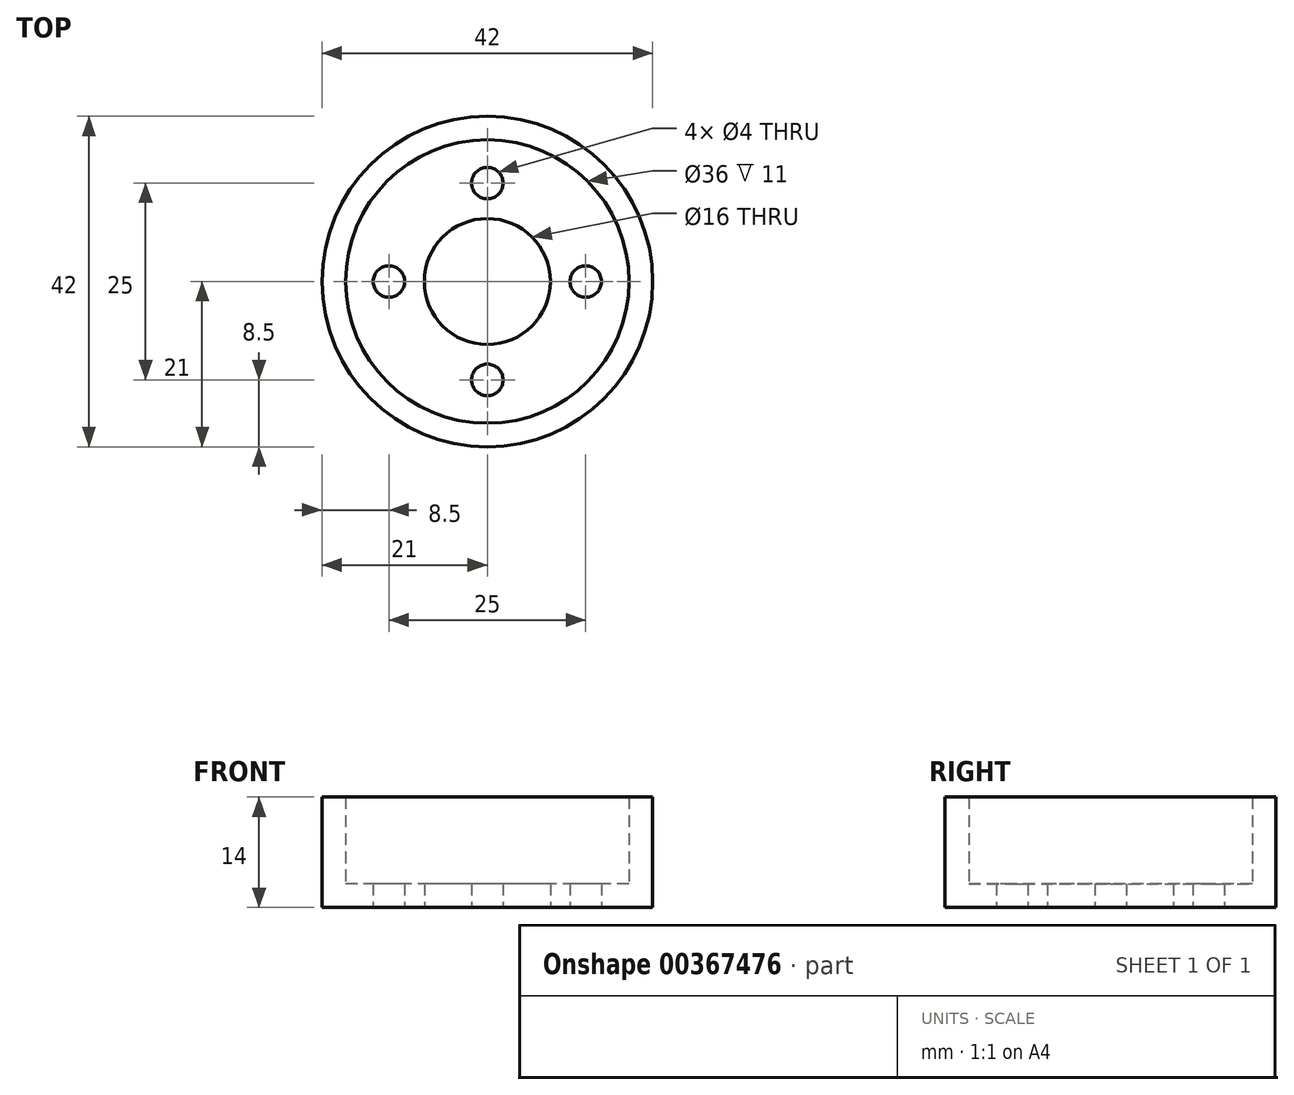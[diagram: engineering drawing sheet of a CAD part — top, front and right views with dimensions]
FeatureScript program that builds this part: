
annotation { "Feature Type Name" : "Feature", "Feature Type Description" : "" }
export const myFeature = defineFeature(function(context is Context, id is Id, definition is map)
    precondition{}
    {
        {
            var Q0;
            Q0=qCreatedBy(makeId("Top.planeOp"),FACE);
            var sketch = newSketch(context, id + "F0", { "sketchPlane" : qUnion([Q0])});
            skLineSegment(sketch, "E0", {"start": v(0, 0) * mm, "end": v(12.5, 0) * mm});
            skCircle(sketch, "E1", {"center": v(12.5, 0) * mm, "radius": 2 * mm});
            skLineSegment(sketch, "E2", {"start": v(0, 0) * mm, "end": v(0, -12.5) * mm});
            skCircle(sketch, "E3", {"center": v(0, -12.5) * mm, "radius": 2 * mm});
            skLineSegment(sketch, "E4", {"start": v(0, 0) * mm, "end": v(0, 12.5) * mm});
            skCircle(sketch, "E5", {"center": v(0, 12.5) * mm, "radius": 2 * mm});
            skLineSegment(sketch, "E6", {"start": v(0, 0) * mm, "end": v(-12.5, 0) * mm});
            skCircle(sketch, "E7", {"center": v(-12.5, 0) * mm, "radius": 2 * mm});
            skSolve(sketch);
        }
        {
            var Q0;
            Q0=qCreatedBy(makeId("Top.planeOp"),FACE);
            var sketch = newSketch(context, id + "F1", { "sketchPlane" : qUnion([Q0])});
            skCircle(sketch, "E8", {"center": v(0, 0) * mm, "radius": 8 * mm});
            skSolve(sketch);
        }
        {
            var Q0;
            Q0=qCreatedBy(makeId("Top.planeOp"),FACE);
            var sketch = newSketch(context, id + "F2", { "sketchPlane" : qUnion([Q0])});
            skCircle(sketch, "E9", {"center": v(0, 0) * mm, "radius": 21 * mm});
            skSolve(sketch);
        }
        {
            var Q0;
            Q0=makeQuery(id+"F2.imprint","IMPRINT",FACE,{"disambiguationData":[TD([[makeQuery(id+"F2.imprint","IMPRINT",EDGE,{"derivedFrom":sQuery(id+"F2.wireOp",EDGE,"E9")}),1.0]])]});
            extrude(context, id + "F3", {"entities" : qUnion([Q0]), "depth" : 14 * mm});
        }
        {
            var Q0;
            Q0=makeQuery(id+"F3.opExtrude","CAP_FACE",FACE,{"disambiguationData":[OSD([sQuery(id+"F2.wireOp",EDGE,"E9")])],"isStart":false});
            shell(context, id + "F4", {"entities" : qUnion([Q0]), "thickness" : 3 * mm});
        }
        {
            var Q0;
            Q0=makeQuery(id+"F1.imprint","IMPRINT",FACE,{"disambiguationData":[TD([[makeQuery(id+"F1.imprint","IMPRINT",EDGE,{"derivedFrom":sQuery(id+"F1.wireOp",EDGE,"E8")}),1.0]])]});
            var sketch = newSketch(context, id + "F5", { "sketchPlane" : qUnion([Q0])});
            skSolve(sketch);
        }
        {
            var Q0;
            Q0=sQuery(id+"F0.wireOp",VERTEX,"E7.center");
            var Q1;
            Q1=sQuery(id+"F0.wireOp",VERTEX,"E5.center");
            var Q2;
            Q2=sQuery(id+"F0.wireOp",VERTEX,"E1.center");
            var Q3;
            Q3=sQuery(id+"F0.wireOp",VERTEX,"E3.center");
            var Q4;
            Q4=makeQuery(id+"F3.opExtrude","SWEPT_BODY",BODY,{"disambiguationData":[OSD([sQuery(id+"F2.wireOp",EDGE,"E9")])]});
            hole(context, id + "F6", {"style" : HoleStyle.SIMPLE, "endStyle" : HoleEndStyle.THROUGH, "oppositeDirection" : true, "holeDiameter" : 4 * mm, "isTappedThrough" : true, "tappedDepth" : 12 * mm, "tapClearance" : 3, "locations" : qUnion([Q0, Q1, Q2, Q3]), "scope" : qUnion([Q4])});
        }
        {
            var Q0;
            Q0=sQuery(id+"F0.wireOp",VERTEX,"E6.start");
            var Q1;
            Q1=makeQuery(id+"F3.opExtrude","SWEPT_BODY",BODY,{"disambiguationData":[OSD([sQuery(id+"F2.wireOp",EDGE,"E9")])]});
            hole(context, id + "F7", {"style" : HoleStyle.SIMPLE, "endStyle" : HoleEndStyle.THROUGH, "oppositeDirection" : true, "holeDiameter" : 16 * mm, "isTappedThrough" : true, "tappedDepth" : 12 * mm, "tapClearance" : 3, "locations" : qUnion([Q0]), "scope" : qUnion([Q1])});
        }
    });
